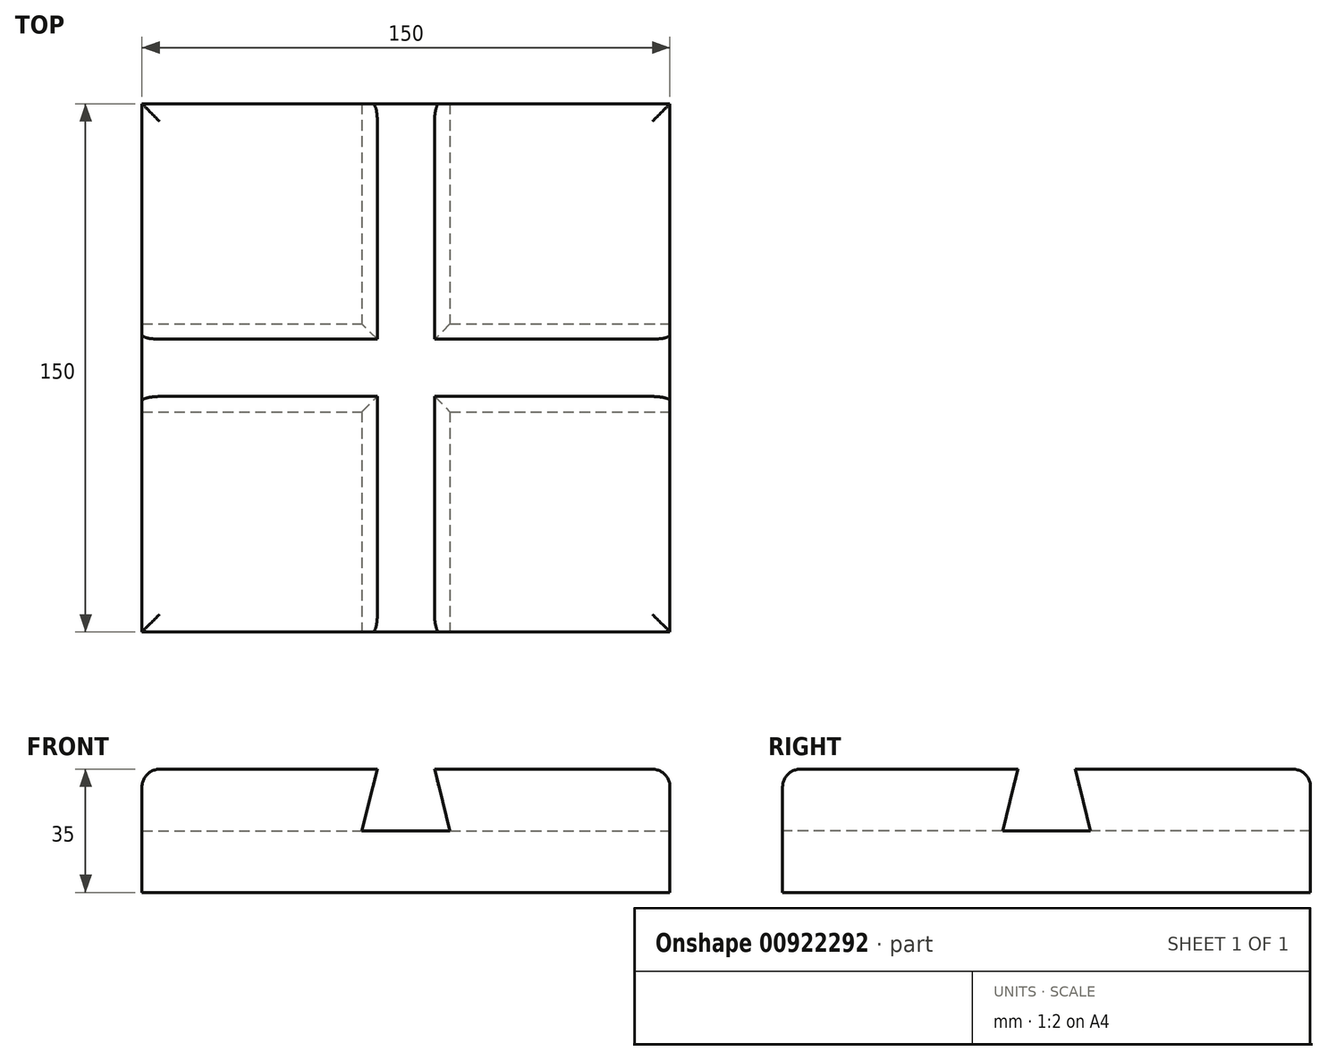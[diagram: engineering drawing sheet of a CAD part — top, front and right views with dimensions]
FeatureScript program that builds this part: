
annotation { "Feature Type Name" : "Feature", "Feature Type Description" : "" }
export const myFeature = defineFeature(function(context is Context, id is Id, definition is map)
    precondition{}
    {
        {
            var Q0;
            Q0=qCreatedBy(makeId("Top.planeOp"),FACE);
            var sketch = newSketch(context, id + "F0", { "sketchPlane" : qUnion([Q0])});
            skLineSegment(sketch, "E0.bottom", {"start": v(75, 75) * mm, "end": v(-75, 75) * mm});
            skLineSegment(sketch, "E0.top", {"start": v(75, -75) * mm, "end": v(-75, -75) * mm});
            skLineSegment(sketch, "E0.left", {"start": v(75, 75) * mm, "end": v(75, -75) * mm});
            skLineSegment(sketch, "E0.right", {"start": v(-75, 75) * mm, "end": v(-75, -75) * mm});
            skPoint(sketch, "E0.middle", {"position": v(0, 0) * mm});
            skSolve(sketch);
        }
        {
            var Q0;
            Q0=makeQuery(id+"F0.imprint","IMPRINT",FACE,{"disambiguationData":[TD([[makeQuery(id+"F0.imprint","IMPRINT",EDGE,{"derivedFrom":sQuery(id+"F0.wireOp",EDGE,"E0.bottom")}),1.0]])]});
            extrude(context, id + "F1", {"entities" : qUnion([Q0]), "endBound" : BoundingType.SYMMETRIC, "depth" : 35 * mm, "offsetDistance" : 25 * mm});
        }
        {
            var Q0;
            Q0=makeQuery(id+"F1.opExtrude","SWEPT_FACE",FACE,{"disambiguationData":[OSD([sQuery(id+"F0.wireOp",EDGE,"E0.top")])]});
            var sketch = newSketch(context, id + "F2", { "sketchPlane" : qUnion([Q0])});
            skLineSegment(sketch, "E1", {"start": v(-12.5, 0) * mm, "end": v(12.5, 0) * mm});
            skLineSegment(sketch, "E2", {"start": v(12.5, 0) * mm, "end": v(8.14, 17.5) * mm});
            skLineSegment(sketch, "E3", {"start": v(8.14, 17.5) * mm, "end": v(-8.14, 17.5) * mm});
            skLineSegment(sketch, "E4", {"start": v(-8.14, 17.5) * mm, "end": v(-12.5, 0) * mm});
            skPoint(sketch, "E5", {"position": v(0, 0) * mm});
            skSolve(sketch);
        }
        {
            var Q0;
            Q0=makeQuery(id+"F2.imprint","IMPRINT",FACE,{"disambiguationData":[TD([[makeQuery(id+"F2.imprint","IMPRINT",EDGE,{"derivedFrom":sQuery(id+"F2.wireOp",EDGE,"E1")}),1.0]])]});
            extrude(context, id + "F3", {"entities" : qUnion([Q0]), "operationType" : NewBodyOperationType.REMOVE, "endBound" : BoundingType.THROUGH_ALL, "oppositeDirection" : true, "depth" : 25 * mm, "offsetDistance" : 25 * mm});
        }
        {
            var Q0;
            Q0=makeQuery(id+"F1.opExtrude","SWEPT_FACE",FACE,{"disambiguationData":[OSD([sQuery(id+"F0.wireOp",EDGE,"E0.left")])]});
            var sketch = newSketch(context, id + "F4", { "sketchPlane" : qUnion([Q0])});
            skLineSegment(sketch, "E6", {"start": v(-12.5, 0) * mm, "end": v(12.5, 0) * mm});
            skLineSegment(sketch, "E7", {"start": v(12.5, 0) * mm, "end": v(8.14, 17.5) * mm});
            skLineSegment(sketch, "E8", {"start": v(8.14, 17.5) * mm, "end": v(-8.14, 17.5) * mm});
            skLineSegment(sketch, "E9", {"start": v(-8.14, 17.5) * mm, "end": v(-12.5, 0) * mm});
            skPoint(sketch, "E10", {"position": v(0, 0) * mm});
            skSolve(sketch);
        }
        {
            var Q0;
            Q0=makeQuery(id+"F4.imprint","IMPRINT",FACE,{"disambiguationData":[TD([[makeQuery(id+"F4.imprint","IMPRINT",EDGE,{"derivedFrom":sQuery(id+"F4.wireOp",EDGE,"E6")}),1.0]])]});
            extrude(context, id + "F5", {"entities" : qUnion([Q0]), "operationType" : NewBodyOperationType.REMOVE, "endBound" : BoundingType.THROUGH_ALL, "oppositeDirection" : true, "depth" : 25 * mm, "offsetDistance" : 25 * mm});
        }
        {
            var Q0;
            {var subQ0=sQuery(id+"F0.wireOp",EDGE,"E0.right");var subQ1=sQuery(id+"F0.wireOp",EDGE,"E0.top");Q0=makeQuery(id+"F5.boolean.opBoolean","SPLIT",EDGE,{"disambiguationData":[TD([makeQuery(id+"F1.opExtrude","SWEPT_FACE",FACE,{"disambiguationData":[OSD([subQ1])]})])],"derivedFrom":makeQuery(id+"F1.opExtrude","CAP_EDGE",EDGE,{"disambiguationData":[OSD([subQ0])],"isStart":false})});}
            var Q1;
            {var subQ0=sQuery(id+"F0.wireOp",EDGE,"E0.right");var subQ1=sQuery(id+"F0.wireOp",EDGE,"E0.top");Q1=makeQuery(id+"F3.boolean.opBoolean","SPLIT",EDGE,{"disambiguationData":[TD([makeQuery(id+"F1.opExtrude","SWEPT_FACE",FACE,{"disambiguationData":[OSD([subQ0])]})])],"derivedFrom":makeQuery(id+"F1.opExtrude","CAP_EDGE",EDGE,{"disambiguationData":[OSD([subQ1])],"isStart":false})});}
            var Q2;
            {var subQ0=sQuery(id+"F0.wireOp",EDGE,"E0.left");var subQ1=sQuery(id+"F0.wireOp",EDGE,"E0.top");Q2=makeQuery(id+"F3.boolean.opBoolean","SPLIT",EDGE,{"disambiguationData":[TD([makeQuery(id+"F1.opExtrude","SWEPT_FACE",FACE,{"disambiguationData":[OSD([subQ0])]})])],"derivedFrom":makeQuery(id+"F1.opExtrude","CAP_EDGE",EDGE,{"disambiguationData":[OSD([subQ1])],"isStart":false})});}
            var Q3;
            {var subQ0=sQuery(id+"F0.wireOp",EDGE,"E0.left");var subQ1=sQuery(id+"F0.wireOp",EDGE,"E0.top");Q3=makeQuery(id+"F5.boolean.opBoolean","SPLIT",EDGE,{"disambiguationData":[TD([makeQuery(id+"F1.opExtrude","SWEPT_FACE",FACE,{"disambiguationData":[OSD([subQ1])]})])],"derivedFrom":makeQuery(id+"F1.opExtrude","CAP_EDGE",EDGE,{"disambiguationData":[OSD([subQ0])],"isStart":false})});}
            var Q4;
            {var subQ0=sQuery(id+"F0.wireOp",EDGE,"E0.bottom");var subQ1=sQuery(id+"F0.wireOp",EDGE,"E0.left");Q4=makeQuery(id+"F5.boolean.opBoolean","SPLIT",EDGE,{"disambiguationData":[TD([makeQuery(id+"F1.opExtrude","SWEPT_FACE",FACE,{"disambiguationData":[OSD([subQ0])]})])],"derivedFrom":makeQuery(id+"F1.opExtrude","CAP_EDGE",EDGE,{"disambiguationData":[OSD([subQ1])],"isStart":false})});}
            var Q5;
            {var subQ0=sQuery(id+"F0.wireOp",EDGE,"E0.bottom");var subQ1=sQuery(id+"F0.wireOp",EDGE,"E0.left");Q5=makeQuery(id+"F3.boolean.opBoolean","SPLIT",EDGE,{"disambiguationData":[TD([makeQuery(id+"F1.opExtrude","SWEPT_FACE",FACE,{"disambiguationData":[OSD([subQ1])]})])],"derivedFrom":makeQuery(id+"F1.opExtrude","CAP_EDGE",EDGE,{"disambiguationData":[OSD([subQ0])],"isStart":false})});}
            var Q6;
            {var subQ0=sQuery(id+"F0.wireOp",EDGE,"E0.bottom");var subQ1=sQuery(id+"F0.wireOp",EDGE,"E0.right");Q6=makeQuery(id+"F3.boolean.opBoolean","SPLIT",EDGE,{"disambiguationData":[TD([makeQuery(id+"F1.opExtrude","SWEPT_FACE",FACE,{"disambiguationData":[OSD([subQ1])]})])],"derivedFrom":makeQuery(id+"F1.opExtrude","CAP_EDGE",EDGE,{"disambiguationData":[OSD([subQ0])],"isStart":false})});}
            var Q7;
            {var subQ0=sQuery(id+"F0.wireOp",EDGE,"E0.bottom");var subQ1=sQuery(id+"F0.wireOp",EDGE,"E0.right");Q7=makeQuery(id+"F5.boolean.opBoolean","SPLIT",EDGE,{"disambiguationData":[TD([makeQuery(id+"F1.opExtrude","SWEPT_FACE",FACE,{"disambiguationData":[OSD([subQ0])]})])],"derivedFrom":makeQuery(id+"F1.opExtrude","CAP_EDGE",EDGE,{"disambiguationData":[OSD([subQ1])],"isStart":false})});}
            fillet(context, id + "F6", {"entities" : qUnion([Q0, Q1, Q2, Q3, Q4, Q5, Q6, Q7]), "radius" : 5 * mm, "tangentPropagation" : true, "allowEdgeOverflow" : false});
        }
    });
